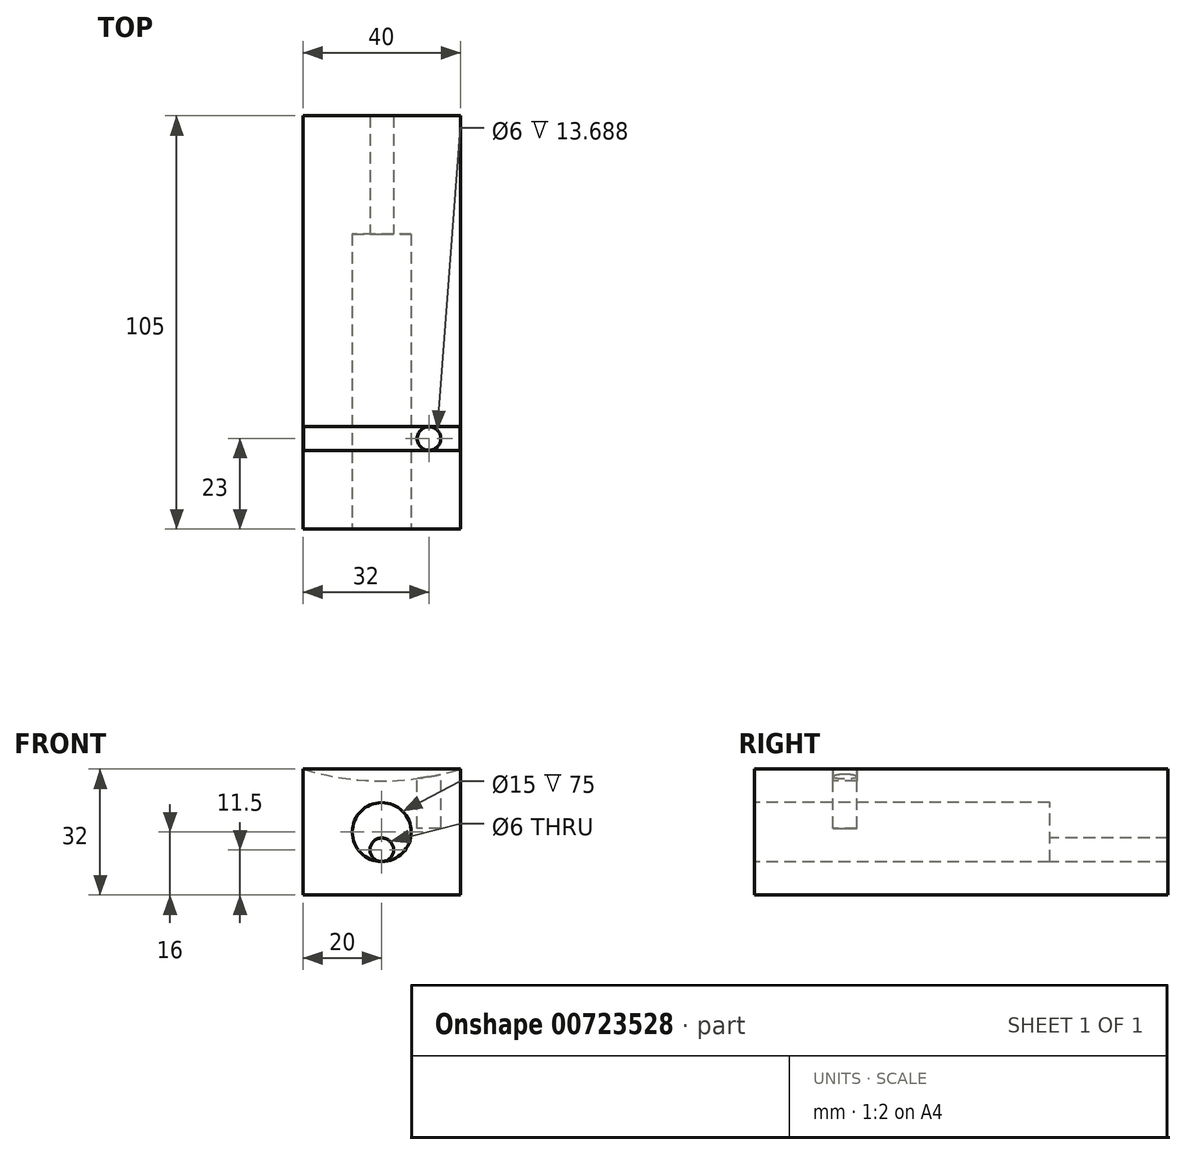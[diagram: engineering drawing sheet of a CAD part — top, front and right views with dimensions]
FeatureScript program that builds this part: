
annotation { "Feature Type Name" : "Feature", "Feature Type Description" : "" }
export const myFeature = defineFeature(function(context is Context, id is Id, definition is map)
    precondition{}
    {
        {
            var Q0;
            Q0=qCreatedBy(makeId("Front.planeOp"),FACE);
            var sketch = newSketch(context, id + "F0", { "sketchPlane" : qUnion([Q0])});
            skLineSegment(sketch, "E0.bottom", {"start": v(0, 0) * mm, "end": v(-40, 0) * mm});
            skLineSegment(sketch, "E0.top", {"start": v(0, 32) * mm, "end": v(-40, 32) * mm});
            skLineSegment(sketch, "E0.left", {"start": v(0, 0) * mm, "end": v(0, 32) * mm});
            skLineSegment(sketch, "E0.right", {"start": v(-40, 0) * mm, "end": v(-40, 32) * mm});
            skSolve(sketch);
        }
        {
            var Q0;
            Q0=qSketchRegion(id+"F0",true);
            extrude(context, id + "F1", {"entities" : qUnion([Q0]), "oppositeDirection" : true, "depth" : 105 * mm, "offsetDistance" : 25 * mm});
        }
        {
            var Q0;
            Q0=makeQuery(id+"F1.opExtrude","CAP_FACE",FACE,{"disambiguationData":[OSD([sQuery(id+"F0.wireOp",EDGE,"E0.bottom"),sQuery(id+"F0.wireOp",EDGE,"E0.top"),sQuery(id+"F0.wireOp",EDGE,"E0.left"),sQuery(id+"F0.wireOp",EDGE,"E0.right")])],"isStart":true});
            var sketch = newSketch(context, id + "F2", { "sketchPlane" : qUnion([Q0])});
            skCircle(sketch, "E1", {"center": v(-20, 16) * mm, "radius": 7.5 * mm});
            skPoint(sketch, "E1.centerSnap0", {"position": v(0, 16) * mm});
            skPoint(sketch, "E1.centerSnap1", {"position": v(-20, 0) * mm});
            skSolve(sketch);
        }
        {
            var Q0;
            Q0=qSketchRegion(id+"F2",true);
            extrude(context, id + "F3", {"entities" : qUnion([Q0]), "operationType" : NewBodyOperationType.REMOVE, "oppositeDirection" : true, "depth" : 75 * mm, "offsetDistance" : 25 * mm});
        }
        {
            var Q0;
            Q0=qCreatedBy(makeId("Front.planeOp"),FACE);
            var sketch = newSketch(context, id + "F4", { "sketchPlane" : qUnion([Q0])});
            skLineSegment(sketch, "E2", {"start": v(0, 0) * mm, "end": v(-20, 0) * mm, "construction": true});
            skLineSegment(sketch, "E3", {"start": v(-20, 0) * mm, "end": v(-20, 16) * mm, "construction": true});
            skLineSegment(sketch, "E4", {"start": v(-20, 16) * mm, "end": v(-20, 8.5) * mm, "construction": true});
            skLineSegment(sketch, "E5", {"start": v(-20, 8.5) * mm, "end": v(-20, 11.5) * mm, "construction": true});
            skCircle(sketch, "E6", {"center": v(-20, 11.5) * mm, "radius": 3 * mm});
            skSolve(sketch);
        }
        {
            var Q0;
            Q0=qSketchRegion(id+"F4",true);
            extrude(context, id + "F5", {"entities" : qUnion([Q0]), "operationType" : NewBodyOperationType.REMOVE, "endBound" : BoundingType.THROUGH_ALL, "oppositeDirection" : true, "depth" : 25 * mm, "offsetDistance" : 25 * mm});
        }
        {
            var Q0;
            Q0=qCreatedBy(makeId("Front.planeOp"),FACE);
            cPlane(context, id + "F6", {"entities" : qUnion([Q0]), "cplaneType" : CPlaneType.OFFSET, "offset" : 20 * mm, "oppositeDirection" : true, "width" : 150 * mm, "height" : 150 * mm});
        }
        {
            var Q0;
            Q0=qCreatedBy(id+"F6.planeOp",FACE);
            var sketch = newSketch(context, id + "F7", { "sketchPlane" : qUnion([Q0])});
            skLineSegment(sketch, "E7", {"start": v(0, 0) * mm, "end": v(0, 32) * mm, "construction": true});
            skLineSegment(sketch, "E8", {"start": v(0, 32) * mm, "end": v(-40, 32) * mm, "construction": true});
            skLineSegment(sketch, "E9", {"start": v(-40, 32) * mm, "end": v(-40, 29) * mm, "construction": true});
            skLineSegment(sketch, "E10", {"start": v(-40, 29) * mm, "end": v(0, 29) * mm, "construction": true});
            skLineSegment(sketch, "E11", {"start": v(-20, 29) * mm, "end": v(-20, 164) * mm, "construction": true});
            skCircle(sketch, "E12", {"center": v(-20, 96.5) * mm, "radius": 67.5 * mm});
            skLineSegment(sketch, "E13", {"start": v(0, 0) * mm, "end": v(-20, 0) * mm, "construction": true});
            skLineSegment(sketch, "E14", {"start": v(-20, 0) * mm, "end": v(-20, 23.5) * mm, "construction": true});
            skSolve(sketch);
        }
        {
            var Q0;
            Q0=qSketchRegion(id+"F7",true);
            extrude(context, id + "F8", {"entities" : qUnion([Q0]), "operationType" : NewBodyOperationType.REMOVE, "oppositeDirection" : true, "depth" : 6 * mm, "offsetDistance" : 25 * mm});
        }
        {
            var Q0;
            {var subQ2=sQuery(id+"F0.wireOp",EDGE,"E0.top");Q0=makeQuery(id+"F8.boolean.opBoolean","SPLIT",FACE,{"disambiguationData":[TD([makeQuery(id+"F8.opExtrude","CAP_FACE",FACE,{"disambiguationData":[OSD([sQuery(id+"F7.wireOp",EDGE,"E12")])],"isStart":false})])],"derivedFrom":makeQuery(id+"F1.opExtrude","SWEPT_FACE",FACE,{"disambiguationData":[OSD([subQ2])]})});}
            cPlane(context, id + "F9", {"entities" : qUnion([Q0]), "cplaneType" : CPlaneType.OFFSET, "offset" : 0 * mm, "width" : 150 * mm, "height" : 150 * mm});
        }
        {
            var Q0;
            Q0=qCreatedBy(id+"F9.planeOp",FACE);
            var sketch = newSketch(context, id + "F10", { "sketchPlane" : qUnion([Q0])});
            skLineSegment(sketch, "E15", {"start": v(0, 0) * mm, "end": v(0, 23) * mm, "construction": true});
            skLineSegment(sketch, "E16", {"start": v(0, 23) * mm, "end": v(-8, 23) * mm, "construction": true});
            skCircle(sketch, "E17", {"center": v(-8, 23) * mm, "radius": 3 * mm});
            skSolve(sketch);
        }
        {
            var Q0;
            Q0 = qSketchRegion(id + "F10", true);
            extrude(context, id + "F11", {"entities" : qUnion([Q0]), "operationType" : NewBodyOperationType.REMOVE, "oppositeDirection" : true, "depth" : 15 * mm, "offsetDistance" : 25 * mm});
        }
    });
